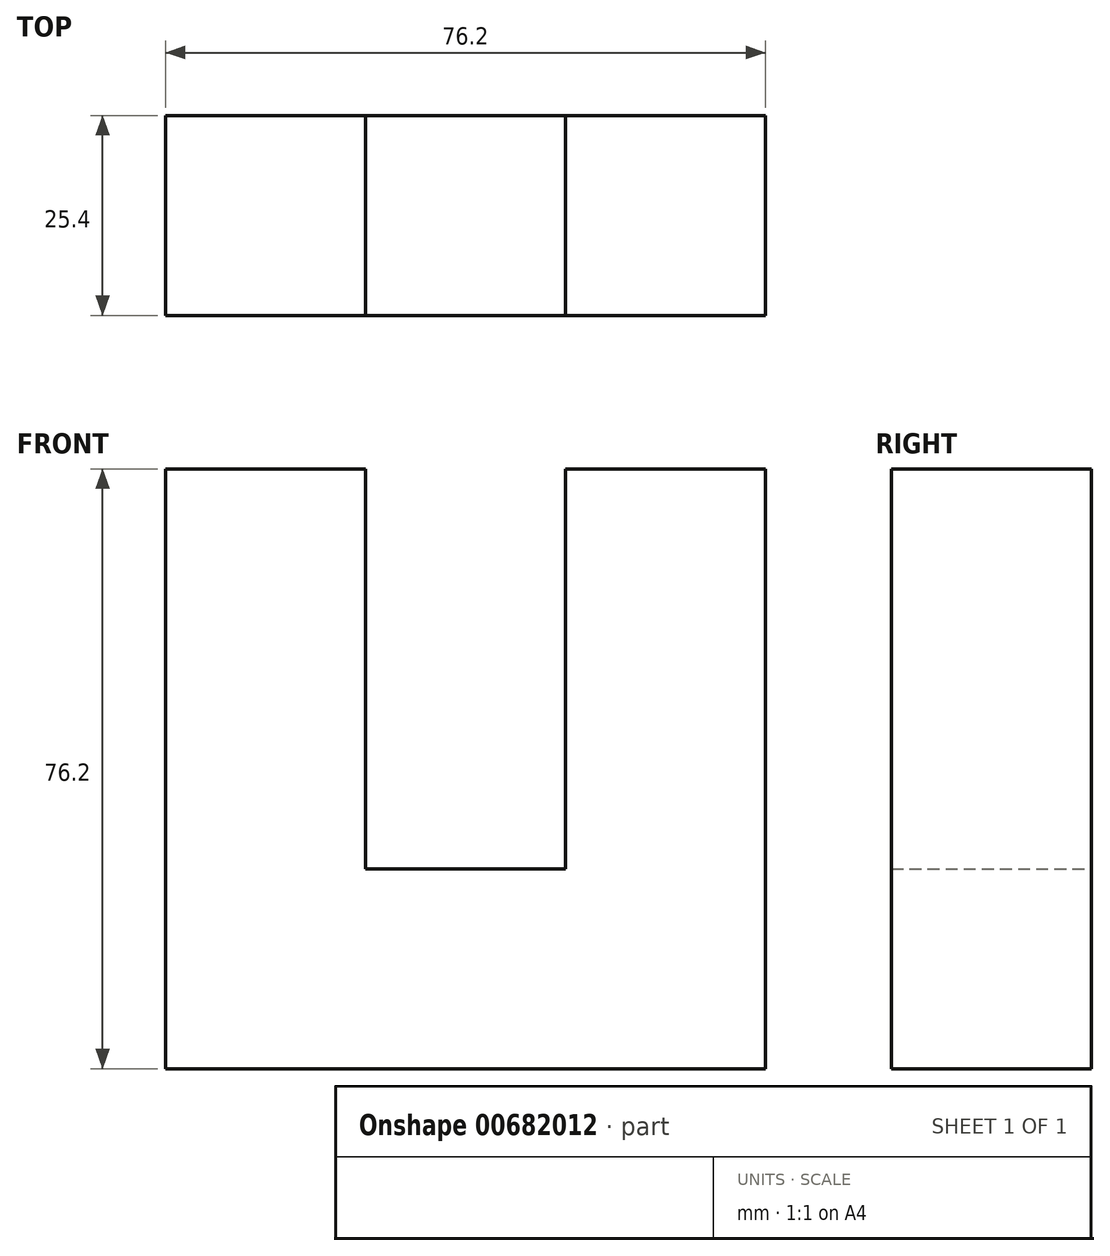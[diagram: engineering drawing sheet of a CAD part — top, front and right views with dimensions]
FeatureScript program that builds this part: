
annotation { "Feature Type Name" : "Feature", "Feature Type Description" : "" }
export const myFeature = defineFeature(function(context is Context, id is Id, definition is map)
    precondition{}
    {
        {
            var Q0;
            Q0=qCreatedBy(makeId("Front.planeOp"),FACE);
            var sketch = newSketch(context, id + "F0", { "sketchPlane" : qUnion([Q0])});
            skLineSegment(sketch, "E0", {"start": v(0, 0) * mm, "end": v(-76.2, 0) * mm});
            skLineSegment(sketch, "E1", {"start": v(-76.2, 0) * mm, "end": v(-76.2, 76.2) * mm});
            skLineSegment(sketch, "E2", {"start": v(-76.2, 76.2) * mm, "end": v(-50.8, 76.2) * mm});
            skLineSegment(sketch, "E3", {"start": v(-50.8, 76.2) * mm, "end": v(-50.8, 25.4) * mm});
            skLineSegment(sketch, "E4", {"start": v(-50.8, 25.4) * mm, "end": v(-25.4, 25.4) * mm});
            skLineSegment(sketch, "E5", {"start": v(-25.4, 25.4) * mm, "end": v(-25.4, 76.2) * mm});
            skLineSegment(sketch, "E6", {"start": v(-25.4, 76.2) * mm, "end": v(0, 76.2) * mm});
            skLineSegment(sketch, "E7", {"start": v(0, 76.2) * mm, "end": v(0, 0) * mm});
            skSolve(sketch);
        }
        {
            var Q0;
            Q0 = qSketchRegion(id + "F0", true);
            extrude(context, id + "F1", {"entities" : qUnion([Q0]), "depth" : 25.4 * mm, "offsetDistance" : 25.4 * mm});
        }
    });
